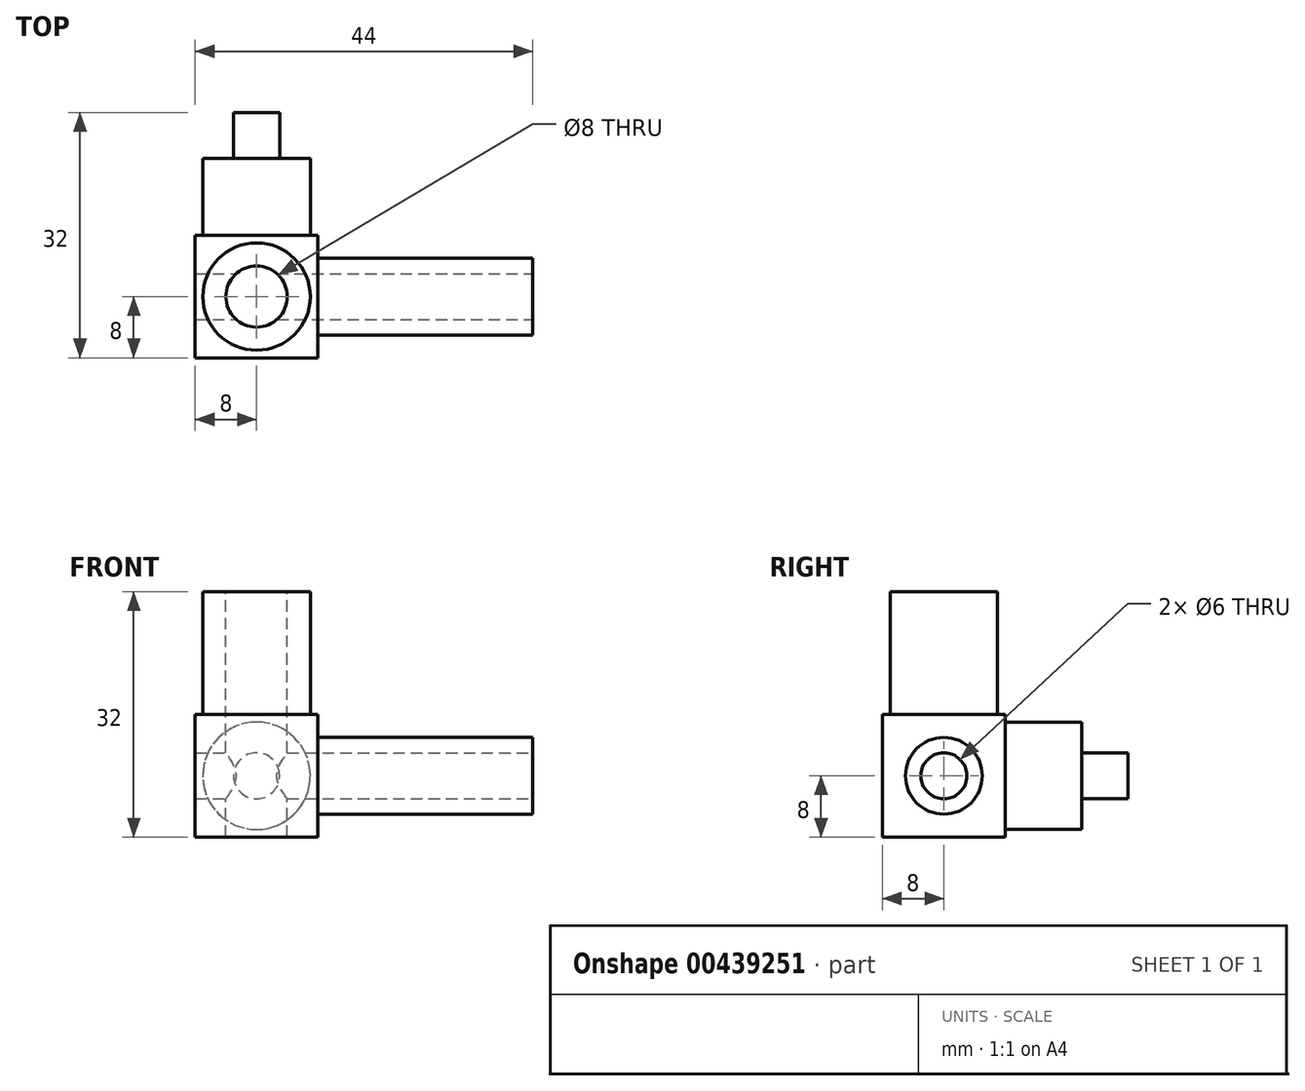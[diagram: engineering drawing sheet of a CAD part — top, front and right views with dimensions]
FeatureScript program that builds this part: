
annotation { "Feature Type Name" : "Feature", "Feature Type Description" : "" }
export const myFeature = defineFeature(function(context is Context, id is Id, definition is map)
    precondition{}
    {
        {
            var Q0;
            Q0=qCreatedBy(makeId("Top.planeOp"),FACE);
            var sketch = newSketch(context, id + "F0", { "sketchPlane" : qUnion([Q0])});
            skLineSegment(sketch, "E0.bottom", {"start": v(8, 8) * mm, "end": v(-8, 8) * mm});
            skLineSegment(sketch, "E0.top", {"start": v(8, -8) * mm, "end": v(-8, -8) * mm});
            skLineSegment(sketch, "E0.left", {"start": v(8, 8) * mm, "end": v(8, -8) * mm});
            skLineSegment(sketch, "E0.right", {"start": v(-8, 8) * mm, "end": v(-8, -8) * mm});
            skPoint(sketch, "E0.middle", {"position": v(0, 0) * mm});
            skSolve(sketch);
        }
        {
            var Q0;
            Q0=makeQuery(id+"F0.imprint","IMPRINT",FACE,{"disambiguationData":[TD([[makeQuery(id+"F0.imprint","IMPRINT",EDGE,{"derivedFrom":sQuery(id+"F0.wireOp",EDGE,"E0.bottom")}),1.0]])]});
            extrude(context, id + "F1", {"entities" : qUnion([Q0]), "depth" : 16 * mm});
        }
        {
            var Q0;
            Q0=makeQuery(id+"F1.opExtrude","SWEPT_FACE",FACE,{"disambiguationData":[OSD([sQuery(id+"F0.wireOp",EDGE,"E0.left")])]});
            var sketch = newSketch(context, id + "F2", { "sketchPlane" : qUnion([Q0])});
            skLineSegment(sketch, "E1", {"start": v(0, 0) * mm, "end": v(0, 20.6) * mm, "construction": true});
            skLineSegment(sketch, "E2", {"start": v(-12.57, 8) * mm, "end": v(13.68, 8) * mm, "construction": true});
            skPoint(sketch, "E2.startSnap0", {"position": v(-8, 8) * mm});
            skCircle(sketch, "E3", {"center": v(0, 8) * mm, "radius": 5 * mm});
            skCircle(sketch, "E4", {"center": v(0, 8) * mm, "radius": 3 * mm});
            skSolve(sketch);
        }
        {
            var Q0;
            Q0=makeQuery(id+"F2.imprint","IMPRINT",FACE,{"disambiguationData":[TD([[makeQuery(id+"F2.imprint","IMPRINT",EDGE,{"derivedFrom":sQuery(id+"F2.wireOp",EDGE,"E4")}),1.0]])]});
            extrude(context, id + "F3", {"entities" : qUnion([Q0]), "operationType" : NewBodyOperationType.REMOVE, "oppositeDirection" : true, "depth" : 25 * mm});
        }
        {
            var Q0;
            Q0=makeQuery(id+"F2.imprint","IMPRINT",FACE,{"disambiguationData":[TD([[makeQuery(id+"F2.imprint","IMPRINT",EDGE,{"derivedFrom":sQuery(id+"F2.wireOp",EDGE,"E3")}),1.0]])]});
            extrude(context, id + "F4", {"entities" : qUnion([Q0]), "operationType" : NewBodyOperationType.ADD, "depth" : 28 * mm});
        }
        {
            var Q0;
            Q0=makeQuery(id+"F1.opExtrude","CAP_FACE",FACE,{"disambiguationData":[OSD([sQuery(id+"F0.wireOp",EDGE,"E0.bottom"),sQuery(id+"F0.wireOp",EDGE,"E0.top"),sQuery(id+"F0.wireOp",EDGE,"E0.left"),sQuery(id+"F0.wireOp",EDGE,"E0.right")])],"isStart":false});
            var sketch = newSketch(context, id + "F5", { "sketchPlane" : qUnion([Q0])});
            skCircle(sketch, "E5", {"center": v(0, 0) * mm, "radius": 7 * mm});
            skCircle(sketch, "E6", {"center": v(0, 0) * mm, "radius": 4 * mm});
            skSolve(sketch);
        }
        {
            var Q0;
            Q0=makeQuery(id+"F5.imprint","IMPRINT",FACE,{"disambiguationData":[TD([[makeQuery(id+"F5.imprint","IMPRINT",EDGE,{"derivedFrom":sQuery(id+"F5.wireOp",EDGE,"E6")}),1.0]])]});
            extrude(context, id + "F6", {"entities" : qUnion([Q0]), "operationType" : NewBodyOperationType.REMOVE, "oppositeDirection" : true, "depth" : 25 * mm});
        }
        {
            var Q0;
            Q0=makeQuery(id+"F5.imprint","IMPRINT",FACE,{"disambiguationData":[TD([[makeQuery(id+"F5.imprint","IMPRINT",EDGE,{"derivedFrom":sQuery(id+"F5.wireOp",EDGE,"E5")}),1.0]])]});
            extrude(context, id + "F7", {"entities" : qUnion([Q0]), "operationType" : NewBodyOperationType.ADD, "depth" : 16 * mm});
        }
        {
            var Q0;
            Q0=makeQuery(id+"F1.opExtrude","SWEPT_FACE",FACE,{"disambiguationData":[OSD([sQuery(id+"F0.wireOp",EDGE,"E0.bottom")])]});
            var sketch = newSketch(context, id + "F8", { "sketchPlane" : qUnion([Q0])});
            skLineSegment(sketch, "E7", {"start": v(0, -3.17) * mm, "end": v(0, 37.2) * mm, "construction": true});
            skLineSegment(sketch, "E8", {"start": v(-11.22, 8) * mm, "end": v(14.76, 8) * mm, "construction": true});
            skPoint(sketch, "E8.startSnap0", {"position": v(-8, 8) * mm});
            skCircle(sketch, "E9", {"center": v(0, 8) * mm, "radius": 7 * mm});
            skCircle(sketch, "E10", {"center": v(0, 8) * mm, "radius": 3 * mm});
            skSolve(sketch);
        }
        {
            var Q0;
            Q0=makeQuery(id+"F8.imprint","IMPRINT",FACE,{"disambiguationData":[TD([[makeQuery(id+"F8.imprint","IMPRINT",EDGE,{"derivedFrom":sQuery(id+"F8.wireOp",EDGE,"E10")}),1.0]])]});
            extrude(context, id + "F9", {"entities" : qUnion([Q0]), "operationType" : NewBodyOperationType.ADD, "depth" : 16 * mm});
        }
        {
            var Q0;
            Q0=makeQuery(id+"F8.imprint","IMPRINT",FACE,{"disambiguationData":[TD([[makeQuery(id+"F8.imprint","IMPRINT",EDGE,{"derivedFrom":sQuery(id+"F8.wireOp",EDGE,"E9")}),1.0]])]});
            extrude(context, id + "F10", {"entities" : qUnion([Q0]), "operationType" : NewBodyOperationType.ADD, "depth" : 10 * mm});
        }
    });
